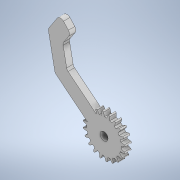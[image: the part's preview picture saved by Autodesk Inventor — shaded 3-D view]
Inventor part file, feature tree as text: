
AUTODESK INVENTOR PART (.ipt)
format: ipt  version: 2021 (Build 250183000, 183)  size: 253,952 bytes
history: native  units: mm
features: extrude x1, sketch x1
ambient origin geometry x8: Origin, YZ Plane, XZ Plane, XY Plane, X Axis, Y Axis, Z Axis, Center Point
bodies: Solid1 (feature_tree)
feature tree (2):
  extrude  "Extrusion1"  Depth=4.0mm
  sketch  "Sketch1"  dims[d0=5.0mm d1=20.0mm d2=24.631832mm d3=4.415mm d4=28.900907mm d5=22.58mm d6=2.5mm d9=21.325522mm d10=11.34mm d12=17.650515mm d13=2.5mm d15=5.75mm d17=9.873328mm d18=2.5mm d22=9.37mm d23=8.3mm d24=8.83mm d25=1.991mm d27=1.018mm d28=180.0mm d30=52.423757mm d32=2.5mm d33=4.0mm d34=0.0mm]
